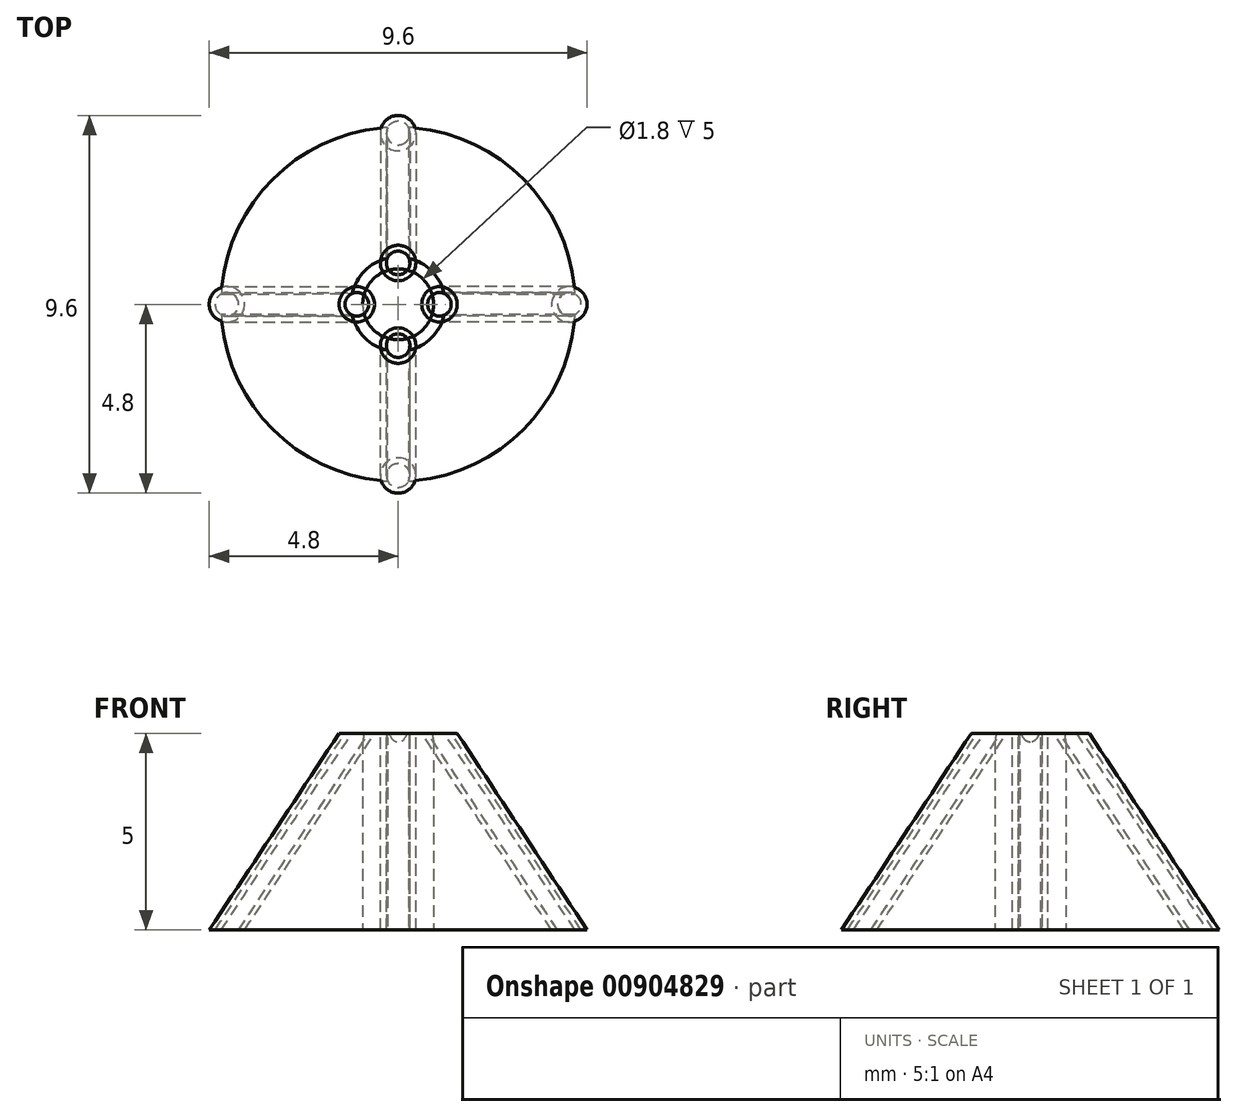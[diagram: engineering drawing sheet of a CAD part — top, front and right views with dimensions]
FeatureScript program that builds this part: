
annotation { "Feature Type Name" : "Feature", "Feature Type Description" : "" }
export const myFeature = defineFeature(function(context is Context, id is Id, definition is map)
    precondition{}
    {
        {
            var Q0;
            Q0=qCreatedBy(makeId("Front.planeOp"),FACE);
            var sketch = newSketch(context, id + "F0", { "sketchPlane" : qUnion([Q0])});
            skLineSegment(sketch, "E0", {"start": v(-0.9, 5) * mm, "end": v(-0.9, 0) * mm});
            skLineSegment(sketch, "E1", {"start": v(-0.9, 0) * mm, "end": v(-4.5, 0) * mm});
            skLineSegment(sketch, "E2", {"start": v(-0.9, 0) * mm, "end": v(0, 0) * mm, "construction": true});
            skLineSegment(sketch, "E3", {"start": v(0, 0) * mm, "end": v(0, 5) * mm, "construction": true});
            skLineSegment(sketch, "E4", {"start": v(0, 5) * mm, "end": v(-0.9, 5) * mm, "construction": true});
            skLineSegment(sketch, "E5", {"start": v(-0.9, 5) * mm, "end": v(-1.2, 5) * mm});
            skLineSegment(sketch, "E6", {"start": v(-1.2, 5) * mm, "end": v(-4.5, 0) * mm});
            skSolve(sketch);
        }
        {
            var Q0;
            Q0=makeQuery(id+"F0.imprint","IMPRINT",FACE,{"disambiguationData":[TD([[makeQuery(id+"F0.imprint","IMPRINT",EDGE,{"derivedFrom":sQuery(id+"F0.wireOp",EDGE,"E0")}),-1.0]])]});
            var Q1;
            Q1=sQuery(id+"F0.wireOp",EDGE,"E3");
            revolve(context, id + "F1", {"surfaceOperationType" : NewSurfaceOperationType.NEW, "entities" : qUnion([Q0]), "axis" : qUnion([Q1]), "revolveType" : RevolveType.FULL});
        }
        {
            var Q0;
            Q0=makeQuery(id+"F1.opRevolve","SWEPT_FACE",FACE,{"disambiguationData":[OSD([sQuery(id+"F0.wireOp",EDGE,"E5")])]});
            var sketch = newSketch(context, id + "F2", { "sketchPlane" : qUnion([Q0])});
            skLineSegment(sketch, "E7", {"start": v(0, 0.9) * mm, "end": v(0, 1.2) * mm, "construction": true});
            skCircle(sketch, "E8", {"center": v(0, 1.05) * mm, "radius": 0.45 * mm});
            skCircle(sketch, "E9", {"center": v(0, 1.05) * mm, "radius": 0.3 * mm});
            skSolve(sketch);
        }
        {
            var Q0;
            Q0=makeQuery(id+"F1.opRevolve","SWEPT_FACE",FACE,{"disambiguationData":[OSD([sQuery(id+"F0.wireOp",EDGE,"E6")])]});
            cPlane(context, id + "F3", {"entities" : qUnion([Q0]), "cplaneType" : CPlaneType.LINE_ANGLE, "offset" : 25 * mm, "angle" : 0 * degree, "width" : 150 * mm, "height" : 150 * mm});
        }
        {
            var Q0;
            Q0=qCreatedBy(id+"F3.planeOp",FACE);
            var sketch = newSketch(context, id + "F4", { "sketchPlane" : qUnion([Q0])});
            skLineSegment(sketch, "E10", {"start": v(1.2, 5) * mm, "end": v(4.5, 0) * mm});
            skLineSegment(sketch, "E11", {"start": v(-4.5, 0) * mm, "end": v(-1.2, 5) * mm});
            skPoint(sketch, "E12.0", {"position": v(-0.9, 5) * mm});
            skLineSegment(sketch, "E13", {"start": v(-0.9, 5) * mm, "end": v(-4.5, 0) * mm});
            skSolve(sketch);
        }
        {
            var Q0;
            {var subQ0=sQuery(id+"F2.wireOp",EDGE,"E8");var subQ1=makeQuery(id+"F1.opRevolve","SWEPT_EDGE",EDGE,{"disambiguationData":[OSD([sQuery(id+"F0.wireOp",EDGE,"E5"),sQuery(id+"F0.wireOp",EDGE,"E6")])]});var subQ2=makeQuery(id+"F2.imprint","INTERSECT",VERTEX,{"disambiguationData":[OD(0.0)],"derivedFrom":[subQ1,subQ0]});Q0=makeQuery(id+"F2.imprint","IMPRINT",FACE,{"disambiguationData":[TD([[makeQuery(id+"F2.imprint","IMPRINT",EDGE,{"disambiguationData":[TD([[subQ2,1.0]])],"derivedFrom":subQ0}),1.0]])]});}
            var Q1;
            {var subQ0=sQuery(id+"F2.wireOp",EDGE,"E8");var subQ1=sQuery(id+"F0.wireOp",EDGE,"E5");var subQ2=makeQuery(id+"F1.opRevolve","SWEPT_EDGE",EDGE,{"disambiguationData":[OSD([subQ1,sQuery(id+"F0.wireOp",EDGE,"E6")])]});var subQ3=makeQuery(id+"F2.imprint","INTERSECT",VERTEX,{"disambiguationData":[OD(0.0)],"derivedFrom":[subQ2,subQ0]});Q1=makeQuery(id+"F2.imprint","IMPRINT",FACE,{"disambiguationData":[TD([[makeQuery(id+"F2.imprint","IMPRINT",EDGE,{"disambiguationData":[TD([[subQ3,-1.0]])],"derivedFrom":subQ0}),1.0]])]});}
            var Q2;
            {var subQ0=sQuery(id+"F2.wireOp",EDGE,"E8");var subQ1=makeQuery(id+"F1.opRevolve","SWEPT_EDGE",EDGE,{"disambiguationData":[OSD([sQuery(id+"F0.wireOp",EDGE,"E0"),sQuery(id+"F0.wireOp",EDGE,"E5")])]});var subQ2=makeQuery(id+"F2.imprint","INTERSECT",VERTEX,{"disambiguationData":[OD(0.0)],"derivedFrom":[subQ1,subQ0]});Q2=makeQuery(id+"F2.imprint","IMPRINT",FACE,{"disambiguationData":[TD([[makeQuery(id+"F2.imprint","IMPRINT",EDGE,{"disambiguationData":[TD([[subQ2,-1.0]])],"derivedFrom":subQ0}),1.0]])]});}
            var Q3;
            {var subQ0=sQuery(id+"F2.wireOp",EDGE,"E8");var subQ1=sQuery(id+"F0.wireOp",EDGE,"E5");var subQ2=makeQuery(id+"F1.opRevolve","SWEPT_EDGE",EDGE,{"disambiguationData":[OSD([subQ1,sQuery(id+"F0.wireOp",EDGE,"E6")])]});var subQ3=makeQuery(id+"F2.imprint","INTERSECT",VERTEX,{"disambiguationData":[OD(1.0)],"derivedFrom":[subQ2,subQ0]});Q3=makeQuery(id+"F2.imprint","IMPRINT",FACE,{"disambiguationData":[TD([[makeQuery(id+"F2.imprint","IMPRINT",EDGE,{"disambiguationData":[TD([[subQ3,1.0]])],"derivedFrom":subQ0}),1.0]])]});}
            var Q4;
            Q4=sQuery(id+"F4.wireOp",EDGE,"E11");
            sweep(context, id + "F5", {"profiles" : qUnion([Q0, Q1, Q2, Q3]), "path" : qUnion([Q4])});
        }
        {
            var Q0;
            {var subQ0=sQuery(id+"F2.wireOp",EDGE,"E9");var subQ1=makeQuery(id+"F1.opRevolve","SWEPT_EDGE",EDGE,{"disambiguationData":[OSD([sQuery(id+"F0.wireOp",EDGE,"E5"),sQuery(id+"F0.wireOp",EDGE,"E6")])]});var subQ2=makeQuery(id+"F2.imprint","INTERSECT",VERTEX,{"disambiguationData":[OD(0.0)],"derivedFrom":[subQ1,subQ0]});Q0=makeQuery(id+"F2.imprint","IMPRINT",FACE,{"disambiguationData":[TD([[makeQuery(id+"F2.imprint","IMPRINT",EDGE,{"disambiguationData":[TD([[subQ2,1.0]])],"derivedFrom":subQ0}),1.0]])]});}
            var Q1;
            {var subQ0=sQuery(id+"F2.wireOp",EDGE,"E9");var subQ1=makeQuery(id+"F1.opRevolve","SWEPT_EDGE",EDGE,{"disambiguationData":[OSD([sQuery(id+"F0.wireOp",EDGE,"E0"),sQuery(id+"F0.wireOp",EDGE,"E5")])]});var subQ2=makeQuery(id+"F2.imprint","INTERSECT",VERTEX,{"disambiguationData":[OD(0.0)],"derivedFrom":[subQ1,subQ0]});Q1=makeQuery(id+"F2.imprint","IMPRINT",FACE,{"disambiguationData":[TD([[makeQuery(id+"F2.imprint","IMPRINT",EDGE,{"disambiguationData":[TD([[subQ2,-1.0]])],"derivedFrom":subQ0}),1.0]])]});}
            var Q2;
            {var subQ0=sQuery(id+"F2.wireOp",EDGE,"E9");var subQ1=sQuery(id+"F0.wireOp",EDGE,"E5");var subQ2=makeQuery(id+"F1.opRevolve","SWEPT_EDGE",EDGE,{"disambiguationData":[OSD([subQ1,sQuery(id+"F0.wireOp",EDGE,"E6")])]});var subQ3=makeQuery(id+"F2.imprint","INTERSECT",VERTEX,{"disambiguationData":[OD(0.0)],"derivedFrom":[subQ2,subQ0]});Q2=makeQuery(id+"F2.imprint","IMPRINT",FACE,{"disambiguationData":[TD([[makeQuery(id+"F2.imprint","IMPRINT",EDGE,{"disambiguationData":[TD([[subQ3,-1.0]])],"derivedFrom":subQ0}),1.0]])]});}
            var Q3;
            Q3=sQuery(id+"F4.wireOp",EDGE,"E11");
            sweep(context, id + "F6", {"operationType" : NewBodyOperationType.REMOVE, "profiles" : qUnion([Q0, Q1, Q2]), "path" : qUnion([Q3])});
        }
        {
            var Q0;
            Q0=makeQuery(id+"F5.opSweep","SWEPT_BODY",BODY,{"disambiguationData":[OSD([sQuery(id+"F2.wireOp",EDGE,"E8"),sQuery(id+"F2.wireOp",EDGE,"E9"),sQuery(id+"F4.wireOp",EDGE,"E11")])]});
            var Q1;
            Q1=makeQuery(id+"F6.boolean.opBoolean","COPY",FACE,{"derivedFrom":makeQuery(id+"F6.opSweep","SWEPT_FACE",FACE,{"disambiguationData":[OSD([sQuery(id+"F2.wireOp",EDGE,"E9"),sQuery(id+"F4.wireOp",EDGE,"E11")])]})});
            var Q2;
            Q2=makeQuery(id+"F1.opRevolve","SWEPT_FACE",FACE,{"disambiguationData":[OSD([sQuery(id+"F0.wireOp",EDGE,"E6")])]});
            circularPattern(context, id + "F7", {"patternType" : PatternType.FACE, "faces" : qUnion([Q1]), "axis" : qUnion([Q2]), "angle" : 360 * degree, "instanceCount" : 4, "equalSpace" : true});
        }
        {
            var Q0;
            Q0=makeQuery(id+"F5.opSweep","SWEPT_BODY",BODY,{"disambiguationData":[OSD([sQuery(id+"F2.wireOp",EDGE,"E8"),sQuery(id+"F2.wireOp",EDGE,"E9"),sQuery(id+"F4.wireOp",EDGE,"E11")])]});
            var Q1;
            Q1=makeQuery(id+"F1.opRevolve","SWEPT_FACE",FACE,{"disambiguationData":[OSD([sQuery(id+"F0.wireOp",EDGE,"E0")])]});
            circularPattern(context, id + "F8", {"entities" : qUnion([Q0]), "axis" : qUnion([Q1]), "angle" : 360 * degree, "instanceCount" : 4, "equalSpace" : true});
        }
    });
